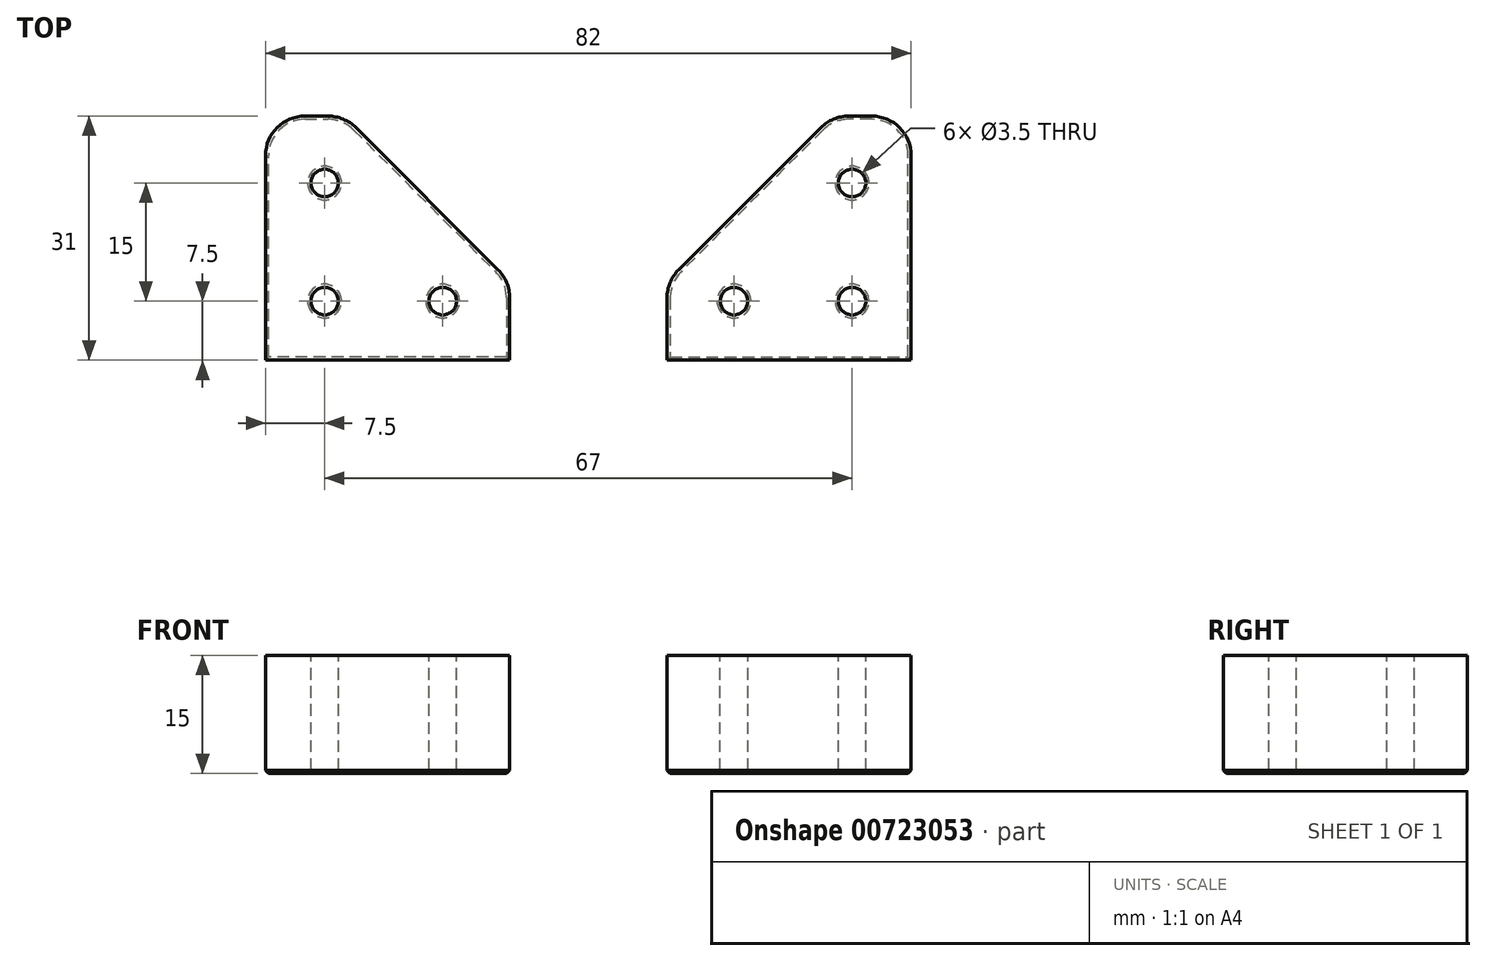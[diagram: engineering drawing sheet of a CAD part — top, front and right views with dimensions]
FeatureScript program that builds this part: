
annotation { "Feature Type Name" : "Feature", "Feature Type Description" : "" }
export const myFeature = defineFeature(function(context is Context, id is Id, definition is map)
    precondition{}
    {
        {
            var Q0;
            Q0=qCreatedBy(makeId("Top.planeOp"),FACE);
            var sketch = newSketch(context, id + "F0", { "sketchPlane" : qUnion([Q0])});
            skLineSegment(sketch, "E0", {"start": v(0, 0) * mm, "end": v(0, 31) * mm});
            skLineSegment(sketch, "E1", {"start": v(0, 31) * mm, "end": v(10, 31) * mm});
            skLineSegment(sketch, "E2", {"start": v(10, 31) * mm, "end": v(31, 10) * mm});
            skLineSegment(sketch, "E3", {"start": v(31, 10) * mm, "end": v(31, 0) * mm});
            skLineSegment(sketch, "E4", {"start": v(31, 0) * mm, "end": v(0, 0) * mm});
            skPoint(sketch, "E5", {"position": v(14.5, 14.5) * mm});
            skLineSegment(sketch, "E6", {"start": v(14.5, 14.5) * mm, "end": v(0, 14.5) * mm, "construction": true});
            skLineSegment(sketch, "E7", {"start": v(14.5, 14.5) * mm, "end": v(14.5, 0) * mm, "construction": true});
            skSolve(sketch);
        }
        {
            var Q0;
            Q0=makeQuery(id+"F0.imprint","IMPRINT",FACE,{"disambiguationData":[TD([[makeQuery(id+"F0.imprint","IMPRINT",EDGE,{"derivedFrom":sQuery(id+"F0.wireOp",EDGE,"E0")}),-1.0]])]});
            extrude(context, id + "F1", {"entities" : qUnion([Q0]), "depth" : 15 * mm, "offsetDistance" : 25 * mm});
        }
        {
            var Q0;
            Q0=makeQuery(id+"F1.opExtrude","CAP_FACE",FACE,{"disambiguationData":[OSD([sQuery(id+"F0.wireOp",EDGE,"E0"),sQuery(id+"F0.wireOp",EDGE,"E1"),sQuery(id+"F0.wireOp",EDGE,"E2"),sQuery(id+"F0.wireOp",EDGE,"E3"),sQuery(id+"F0.wireOp",EDGE,"E4")])],"isStart":false});
            var sketch = newSketch(context, id + "F2", { "sketchPlane" : qUnion([Q0])});
            skLineSegment(sketch, "E8", {"start": v(7.5, 22.5) * mm, "end": v(7.5, 7.5) * mm, "construction": true});
            skLineSegment(sketch, "E9", {"start": v(7.5, 7.5) * mm, "end": v(22.5, 7.5) * mm, "construction": true});
            skLineSegment(sketch, "E10", {"start": v(7.5, 7.5) * mm, "end": v(7.5, 0) * mm, "construction": true});
            skLineSegment(sketch, "E11", {"start": v(7.5, 7.5) * mm, "end": v(0, 7.5) * mm, "construction": true});
            skCircle(sketch, "E12", {"center": v(7.5, 22.5) * mm, "radius": 1.75 * mm});
            skCircle(sketch, "E13", {"center": v(7.5, 7.5) * mm, "radius": 1.75 * mm});
            skCircle(sketch, "E14", {"center": v(22.5, 7.5) * mm, "radius": 1.75 * mm});
            skSolve(sketch);
        }
        {
            var Q0;
            Q0=qSketchRegion(id+"F2",true);
            extrude(context, id + "F3", {"entities" : qUnion([Q0]), "operationType" : NewBodyOperationType.REMOVE, "endBound" : BoundingType.UP_TO_NEXT, "oppositeDirection" : true, "depth" : 25 * mm});
        }
        {
            var Q0;
            Q0=makeQuery(id+"F1.opExtrude","CAP_FACE",FACE,{"disambiguationData":[OSD([sQuery(id+"F0.wireOp",EDGE,"E0"),sQuery(id+"F0.wireOp",EDGE,"E1"),sQuery(id+"F0.wireOp",EDGE,"E2"),sQuery(id+"F0.wireOp",EDGE,"E3"),sQuery(id+"F0.wireOp",EDGE,"E4")])],"isStart":true});
            var sketch = newSketch(context, id + "F4", { "sketchPlane" : qUnion([Q0])});
            skLineSegment(sketch, "E15.bottom", {"start": v(0, 0) * mm, "end": v(31, 0) * mm});
            skLineSegment(sketch, "E15.top", {"start": v(0, 31) * mm, "end": v(31, 31) * mm});
            skLineSegment(sketch, "E15.left", {"start": v(0, 0) * mm, "end": v(0, 31) * mm});
            skLineSegment(sketch, "E15.right", {"start": v(31, 0) * mm, "end": v(31, 31) * mm});
            skPoint(sketch, "E16", {"position": v(14.5, 15.5) * mm});
            skLineSegment(sketch, "E17", {"start": v(14.5, 0) * mm, "end": v(14.5, 31) * mm, "construction": true});
            skSolve(sketch);
        }
        {
            var Q0;
            Q0=makeQuery(id+"F1.opExtrude","SWEPT_EDGE",EDGE,{"disambiguationData":[OSD([sQuery(id+"F0.wireOp",EDGE,"E2"),sQuery(id+"F0.wireOp",EDGE,"E3")])]});
            var Q1;
            Q1=makeQuery(id+"F1.opExtrude","SWEPT_EDGE",EDGE,{"disambiguationData":[OSD([sQuery(id+"F0.wireOp",EDGE,"E1"),sQuery(id+"F0.wireOp",EDGE,"E2")])]});
            var Q2;
            Q2=makeQuery(id+"F1.opExtrude","SWEPT_EDGE",EDGE,{"disambiguationData":[OSD([sQuery(id+"F0.wireOp",EDGE,"E0"),sQuery(id+"F0.wireOp",EDGE,"E1")])]});
            fillet(context, id + "F5", {"entities" : qUnion([Q0, Q1, Q2]), "radius" : 5 * mm, "tangentPropagation" : true, "allowEdgeOverflow" : false});
        }
        {
            var Q0;
            Q0=makeQuery(id+"FCIbPaHNMw7s3Ox_1.boolean.opBoolean","MERGE",FACE,{"derivedFrom":[makeQuery(id+"F1.opExtrude","CAP_FACE",FACE,{"disambiguationData":[OSD([sQuery(id+"F0.wireOp",EDGE,"E0"),sQuery(id+"F0.wireOp",EDGE,"E1"),sQuery(id+"F0.wireOp",EDGE,"E2"),sQuery(id+"F0.wireOp",EDGE,"E3"),sQuery(id+"F0.wireOp",EDGE,"E4")])],"isStart":true}),makeQuery(id+"FCIbPaHNMw7s3Ox_1.opExtrude","CAP_FACE",FACE,{"disambiguationData":[OSD([sQuery(id+"F4.wireOp",EDGE,"E15.bottom"),sQuery(id+"F4.wireOp",EDGE,"E15.top"),sQuery(id+"F4.wireOp",EDGE,"E15.left"),sQuery(id+"F4.wireOp",EDGE,"E15.right")])],"isStart":true})]});
            chamfer(context, id + "F6", {"entities" : qUnion([Q0]), "chamferType" : ChamferType.OFFSET_ANGLE, "width" : 0.4 * mm, "oppositeDirection" : false, "angle" : 45 * degree, "tangentPropagation" : true});
        }
        {
            var Q0;
            Q0=makeQuery(id+"FCIbPaHNMw7s3Ox_1.boolean.opBoolean","MERGE",FACE,{"derivedFrom":[makeQuery(id+"F1.opExtrude","SWEPT_FACE",FACE,{"disambiguationData":[OSD([sQuery(id+"F0.wireOp",EDGE,"E3")])]}),makeQuery(id+"FCIbPaHNMw7s3Ox_1.opExtrude","SWEPT_FACE",FACE,{"disambiguationData":[OSD([sQuery(id+"F4.wireOp",EDGE,"E15.right")])]})]});
            cPlane(context, id + "F7", {"entities" : qUnion([Q0]), "cplaneType" : CPlaneType.OFFSET, "offset" : 10 * mm, "width" : 150 * mm, "height" : 150 * mm});
        }
        {
            var Q0;
            Q0=makeQuery(id+"F1.opExtrude","SWEPT_BODY",BODY,{"disambiguationData":[OSD([sQuery(id+"F0.wireOp",EDGE,"E0"),sQuery(id+"F0.wireOp",EDGE,"E1"),sQuery(id+"F0.wireOp",EDGE,"E2"),sQuery(id+"F0.wireOp",EDGE,"E3"),sQuery(id+"F0.wireOp",EDGE,"E4")])]});
            var Q1;
            Q1=qCreatedBy(id+"F7.planeOp",FACE);
            mirror(context, id + "F8", {"entities" : qUnion([Q0]), "mirrorPlane" : qUnion([Q1])});
        }
    });
